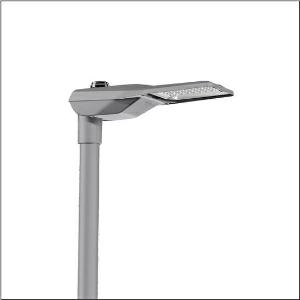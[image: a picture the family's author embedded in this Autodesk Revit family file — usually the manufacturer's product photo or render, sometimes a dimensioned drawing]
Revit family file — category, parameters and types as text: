
# Revit family: streetlight_sl_21_mini___st0_5a_5xe6b37n08gb_187f
name_source: partatom
category: Lighting Fixtures
units: mm (PartAtom-declared; Revit-internal decimal feet)

## family parameters
Cut with Voids When Loaded = No
Host = Face
Light Source = No
Part Type = Normal
Room Calculation Point = No
Round Connector Dimension = Use Diameter
Shared = No

## types (1)
- --- (1 x LED, 5940 lm, 40.4 W, 3000K)
    Apparent Load = 40 VA
    CIE Flux Codes = 41 75 97 100 100
    Color Rendering = 70
    Color Temperature = 3000K
    Default Elevation = 1800 mm
    Description = Streetlight SL 21 mini, mast luminaire, primary light control with lens, of PMMA, primary optical cover: cover, of toughened safety glass, transparent, light distribution: ST0.5a, light emission: direct distribution, primary light characteristic: asymmetric, installation type: side-entry, LED, 3G 1.5mm², High Power LED, rated luminous flux: 5.940lm, luminous efficacy: 147lm/W, light colour: 730, colour temperature: 3000K, control: overheat protection, presetting dimming linear, constant luminous flux control, time-dependent luminous flux control, flexible luminous flux parameterisation, mains connection: 230..240V, AC, 50/60Hz, connection cable pre-assembled, cable length: 8,5m, wiring characteristics: H07RN-F, start of lifetime: 40W, end of service life: 41W, reduction: 19W, luminaire housing, of diecast aluminium (EN AC-44300), powder-coated, Siteco® metallic grey (DB 702S), corrosivity category C5 mid according to DIN EN ISO 12944, multi-level sealing system, sealing non-destructively replaceable, inclination adjustable: 0°, 5°, 10°, 15°, length: 628mm, width: 235mm, height: 110mm, spigot size: 42mm (side-entry), protection rating (complete): IP66, insulation class (complete): insulation class I (protective earthing), certification: CE, ENEC, ENEC+, VDE, impact resistance: IK09, permissible operating ambient temperature for outdoor applications: -40..+50°C, standard-compliant lighting for roads and squares, packaging unit: 1 piece

Light Distribution: ST0.5a
    Height = 110 mm
    Lamp = 1 x LED
    Lamp Light Flux = 5940 lm
    Lamp Power = 40.4 W
    Lamp count = 1
    Length = 625 mm
    Luminous efficacy = 147 lm/W
    Manufacturer = Siteco
    ModVariant = No
    Model = 5XE6B37N08GB
    Number of Poles = 1
    OnlyDefault = Yes
    Power Factor = 1
    Product Name = Streetlight SL 21 mini | ST0.5a
    Product group = mast luminaire | pylon top
    ProductGroupID = 6100
    Protection Class = Protection class I
    Protection Degree = IP 66
    RLX_Detail_Level = 1
    RLX_Emergency_Light_Flux = 0 lm
    RLX_Emergency_Type = 0
    RLX_Emergency_Type_DB = No
    RlxData = <blob elided: 102841 chars, md5=d4f4bd98>
    Socket = socket
    Standby Power = 0 W
    System Light Flux = 5940 lm
    System Power = 40 W
    Type Comments = factory setting: luminous flux: 100 % | dim-lin: 254 | 812 mA
    Type Image = l_1294379.jpg
    URL = http://relux.com
    VarID = @adj_068869
    Voltage = 0 V
    Weight = 0.00 kg
    Width = 234 mm

## geometry (parser evidence)
native form markers: Blend x4, Sweep x10
no freeform markers — native parametric forms only
